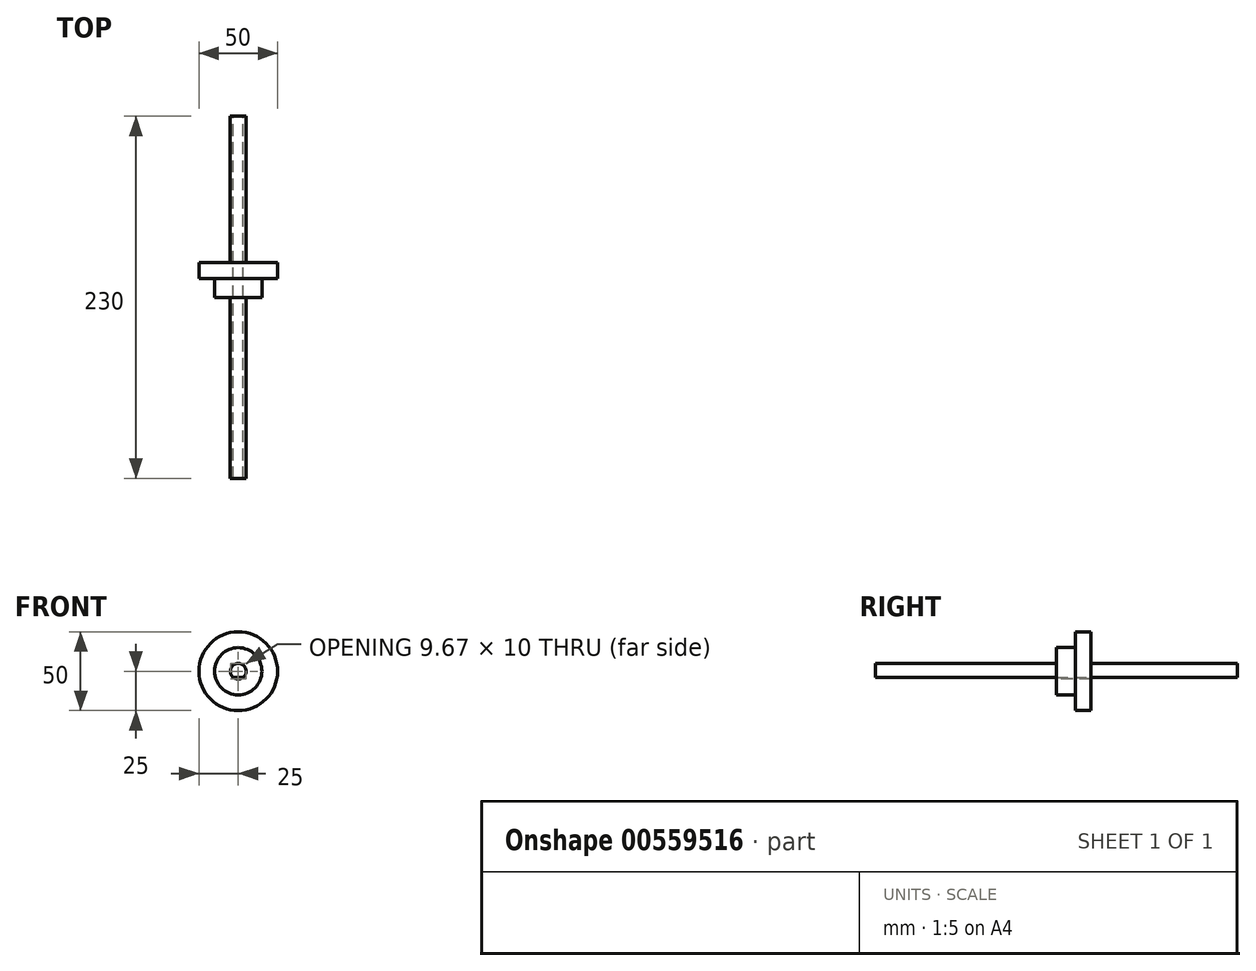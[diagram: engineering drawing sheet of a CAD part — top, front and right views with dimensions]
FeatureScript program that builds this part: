
annotation { "Feature Type Name" : "Feature", "Feature Type Description" : "" }
export const myFeature = defineFeature(function(context is Context, id is Id, definition is map)
    precondition{}
    {
        {
            var Q0;
            Q0=qCreatedBy(makeId("Front.planeOp"),FACE);
            var sketch = newSketch(context, id + "F0", { "sketchPlane" : qUnion([Q0])});
            skCircle(sketch, "E0", {"center": v(0, 0) * mm, "radius": 5 * mm});
            skLineSegment(sketch, "E1", {"start": v(-3.23, -3.81) * mm, "end": v(3.23, -3.81) * mm});
            skSolve(sketch);
        }
        {
            var Q0;
            {var subQ0=sQuery(id+"F0.wireOp",EDGE,"E1");Q0=makeQuery(id+"F0.imprint","IMPRINT",FACE,{"disambiguationData":[TD([[makeQuery(id+"F0.imprint","IMPRINT",EDGE,{"derivedFrom":subQ0}),1.0]])]});}
            extrude(context, id + "F1", {"entities" : qUnion([Q0]), "endBound" : BoundingType.SYMMETRIC, "depth" : 230 * mm, "offsetDistance" : 25 * mm});
        }
        {
            var Q0;
            Q0=qCreatedBy(makeId("Right.planeOp"),FACE);
            var sketch = newSketch(context, id + "F2", { "sketchPlane" : qUnion([Q0])});
            skLineSegment(sketch, "E2", {"start": v(0, 0) * mm, "end": v(-38.9, 0) * mm, "construction": true});
            skLineSegment(sketch, "E3", {"start": v(-38.9, 0) * mm, "end": v(32.06, 0) * mm, "construction": true});
            skLineSegment(sketch, "E4", {"start": v(22, 0) * mm, "end": v(22, 25) * mm});
            skLineSegment(sketch, "E5", {"start": v(22, 25) * mm, "end": v(12, 25) * mm});
            skLineSegment(sketch, "E6", {"start": v(12, 25) * mm, "end": v(12, 15) * mm});
            skLineSegment(sketch, "E7", {"start": v(12, 15) * mm, "end": v(0, 15) * mm});
            skLineSegment(sketch, "E8", {"start": v(0, 15) * mm, "end": v(0, 0) * mm});
            skLineSegment(sketch, "E9", {"start": v(22, 5.25) * mm, "end": v(-7.97, 5.25) * mm});
            skLineSegment(sketch, "E10", {"start": v(-115, 5) * mm, "end": v(115, 5) * mm});
            skSolve(sketch);
        }
        {
            var Q0;
            Q0 = qSketchRegion(id + "F2", true);
            var Q1;
            Q1=sQuery(id+"F2.wireOp",EDGE,"E3");
            revolve(context, id + "F3", {"operationType" : NewBodyOperationType.ADD, "entities" : qUnion([Q0]), "axis" : qUnion([Q1]), "revolveType" : RevolveType.FULL});
        }
    });
